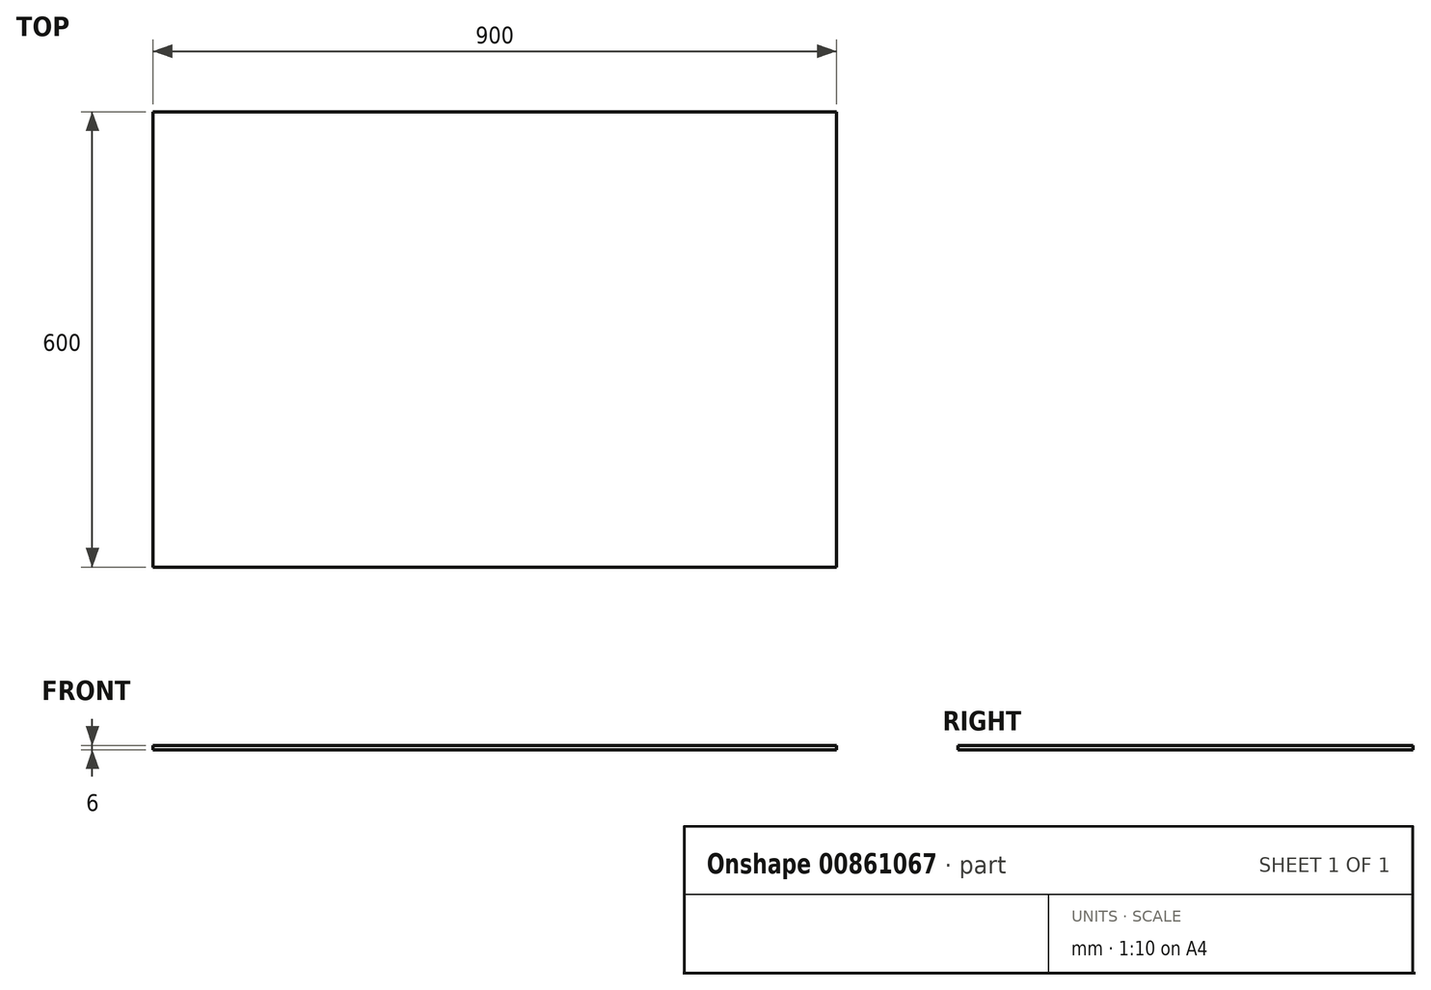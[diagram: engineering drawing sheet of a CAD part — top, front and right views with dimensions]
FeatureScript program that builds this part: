
annotation { "Feature Type Name" : "Feature", "Feature Type Description" : "" }
export const myFeature = defineFeature(function(context is Context, id is Id, definition is map)
    precondition{}
    {
        {
            var Q0;
            Q0=qCreatedBy(makeId("Top.planeOp"),FACE);
            var sketch = newSketch(context, id + "F0", { "sketchPlane" : qUnion([Q0])});
            skLineSegment(sketch, "E0.bottom", {"start": v(450, -300) * mm, "end": v(-450, -300) * mm});
            skLineSegment(sketch, "E0.top", {"start": v(450, 300) * mm, "end": v(-450, 300) * mm});
            skLineSegment(sketch, "E0.left", {"start": v(450, -300) * mm, "end": v(450, 300) * mm});
            skLineSegment(sketch, "E0.right", {"start": v(-450, -300) * mm, "end": v(-450, 300) * mm});
            skPoint(sketch, "E0.middle", {"position": v(0, 0) * mm});
            skSolve(sketch);
        }
        {
            var Q0;
            Q0=makeQuery(id+"F0.imprint","IMPRINT",FACE,{"disambiguationData":[TD([[makeQuery(id+"F0.imprint","IMPRINT",EDGE,{"derivedFrom":sQuery(id+"F0.wireOp",EDGE,"E0.bottom")}),-1.0]])]});
            extrude(context, id + "F1", {"entities" : qUnion([Q0]), "depth" : 6 * mm, "offsetDistance" : 25 * mm, "symmetric" : true});
        }
    });
